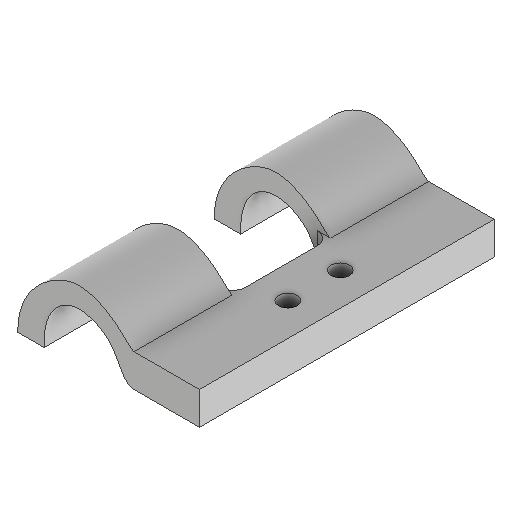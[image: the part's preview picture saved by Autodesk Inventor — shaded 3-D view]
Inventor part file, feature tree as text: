
AUTODESK INVENTOR PART (.ipt)
format: ipt  version: 2024.1 (Build 281209000, 209)  size: 177,152 bytes
history: native  units: mm
features: reference x4, extrude x3, sketch x3, projected_geometry x2, other x2, fillet x1
ambient origin geometry x8: Origin, YZ Plane, XZ Plane, XY Plane, X Axis, Y Axis, Z Axis, Center Point
bodies: Volumenkörper1 (feature_tree)
feature tree (15):
  extrude  "Extrusion1"  Depth=10.0mm
  extrude  "Extrusion2"  Depth=5.0mm TaperAngle=0.0deg
  extrude  "Extrusion3"  TaperAngle=0.0deg  [1 undecoded]
  fillet  "Rundung1"  Radius=2.0mm
  sketch  "Skizze1"  dims[d0=10.0mm d1=45.0mm]
  reference  "Referenz1"
  reference  "Referenz2"
  reference  "Referenz3"
  reference  "Referenz4"
  sketch  "Skizze2"  dims[d2=5.0mm d3=0.0mm d4=5.0mm d5=0.0mm]
  projected_geometry  "Projizierte Kontur1"
  sketch  "Skizze3"  dims[d6=15.0mm d7=0.0mm d8=0.0mm d9=2.0mm]
  projected_geometry  "Projizierte Kontur2"
  other  "Assembly_Planktoscope_Uc2version_wormdrive_V3.iam"
  other  "60_Planktoscope_Sampleholder:1"
note: 1 required parameter value undecoded (feature->parameter linkage not recoverable at this tier; creation-order binding heuristic only, values carry confidence <= 0.55)
